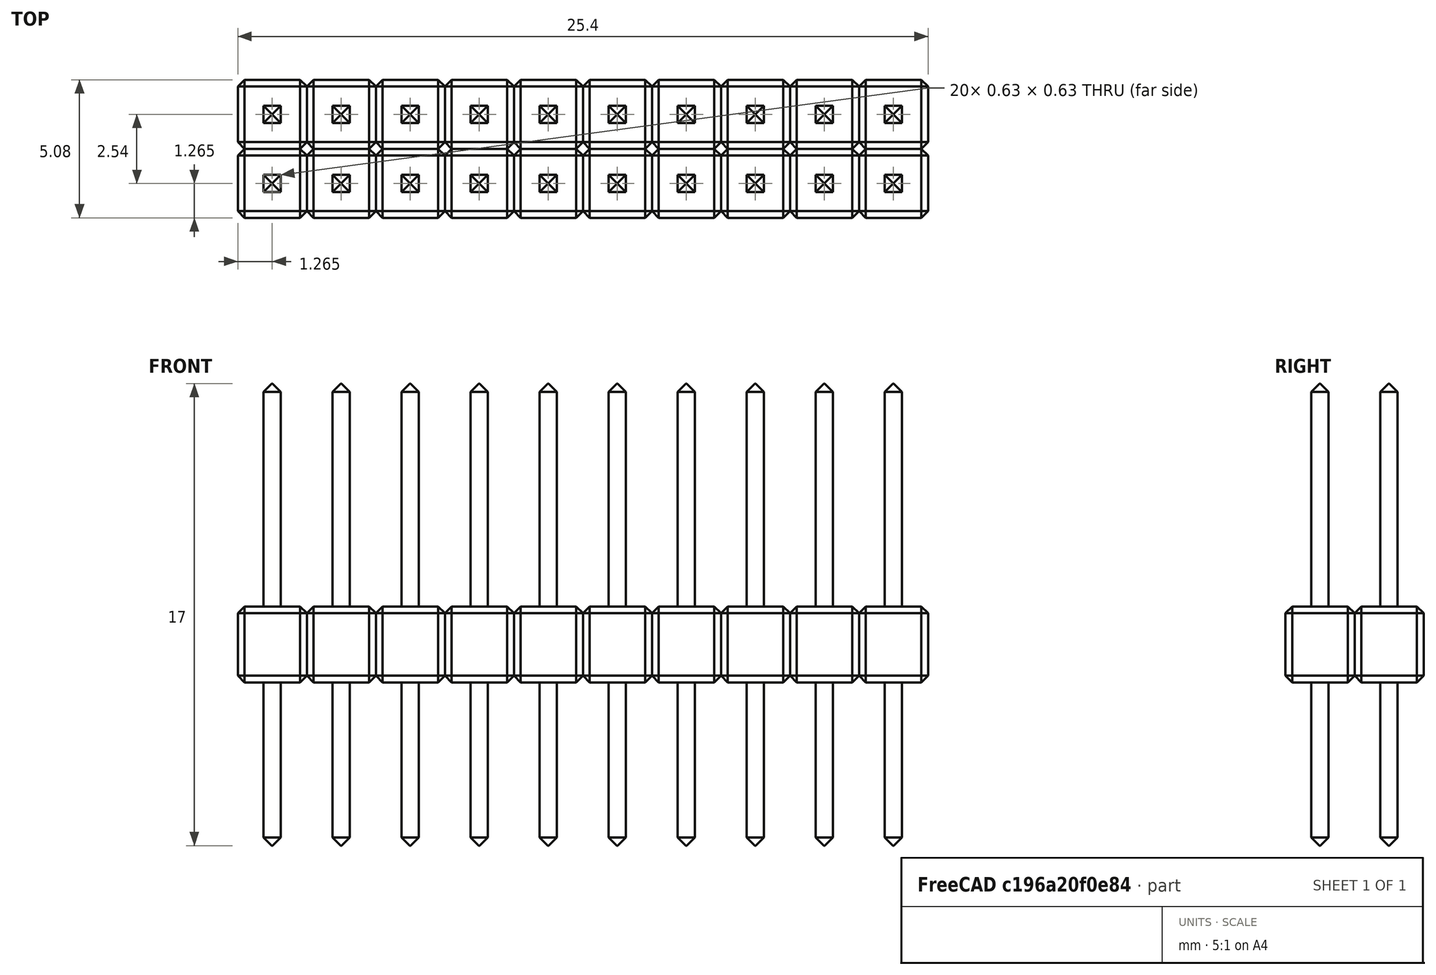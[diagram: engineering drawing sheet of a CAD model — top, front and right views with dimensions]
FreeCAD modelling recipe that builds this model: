
FCSTD DOCUMENT  (FreeCAD 0.18R4 (GitTag))
Label: 20 Pin Header Dual Row
License: All rights reserved
LicenseURL: http://en.wikipedia.org/wiki/All_rights_reserved
objects: Part::Box×2, Part::Chamfer×2, Part::FeaturePython×2, Part::MultiFuse×1
note: 7 computed .brp shape members not serialized (recipe doc carries the construction recipe); baked Part::Feature solids carry a one-line shape summary decoded from their .brp

FEATURE [Part::Box] Box001  label="Cube001"
  AttacherType = Attacher::AttachEngine3D
  Height = 17
  Length = 0.63
  Placement = pos=(-3,0,0) rot=(0,0,1;0rad)
  Width = 0.63
FEATURE [Part::Box] Box  label="Cube"
  AttacherType = Attacher::AttachEngine3D
  Height = 2.8
  Length = 2.54
  Width = 2.54
FEATURE [Part::Chamfer] Chamfer  label="Body"
  Base = -> Box
  Edges = 12 edges r=0.25: [Edge1,Edge2,Edge3,Edge4,Edge5,Edge6,Edge7,Edge8,Edge9,Edge10,Edge11,Edge12]
FEATURE [Part::FeaturePython] Array  label="Bodies"  # Draft array (typed FeaturePython)
  Angle = 360
  ArrayType = 0
  Axis = (0,0,1)
  Base = -> Chamfer
  Center = (0,0,0)
  Fuse = false
  IntervalAxis = (0,0,0)
  IntervalX = (2.54,0,0)
  IntervalY = (0,2.54,0)
  IntervalZ = (0,0,1)
  NumberPolar = 1
  NumberX = 10
  NumberY = 2
  NumberZ = 1
FEATURE [Part::Chamfer] Chamfer001  label="Pin"
  Base = -> Box001
  Edges = 8 edges r=0.3: [Edge2,Edge4,Edge6,Edge8,Edge9,Edge10,Edge11,Edge12]
  Placement = pos=(3.95,0.95,-6) rot=(0,0,1;0rad)
FEATURE [Part::FeaturePython] Array001  label="Pins"  # Draft array (typed FeaturePython)
  Angle = 360
  ArrayType = 0
  Axis = (0,0,1)
  Base = -> Chamfer001
  Center = (0,0,0)
  Fuse = false
  IntervalAxis = (0,0,0)
  IntervalX = (2.54,0,0)
  IntervalY = (0,2.54,0)
  IntervalZ = (0,0,1)
  NumberPolar = 1
  NumberX = 10
  NumberY = 2
  NumberZ = 1
FEATURE [Part::MultiFuse] Fusion  label="Header"
  Shapes = -> [Array001,Array]
